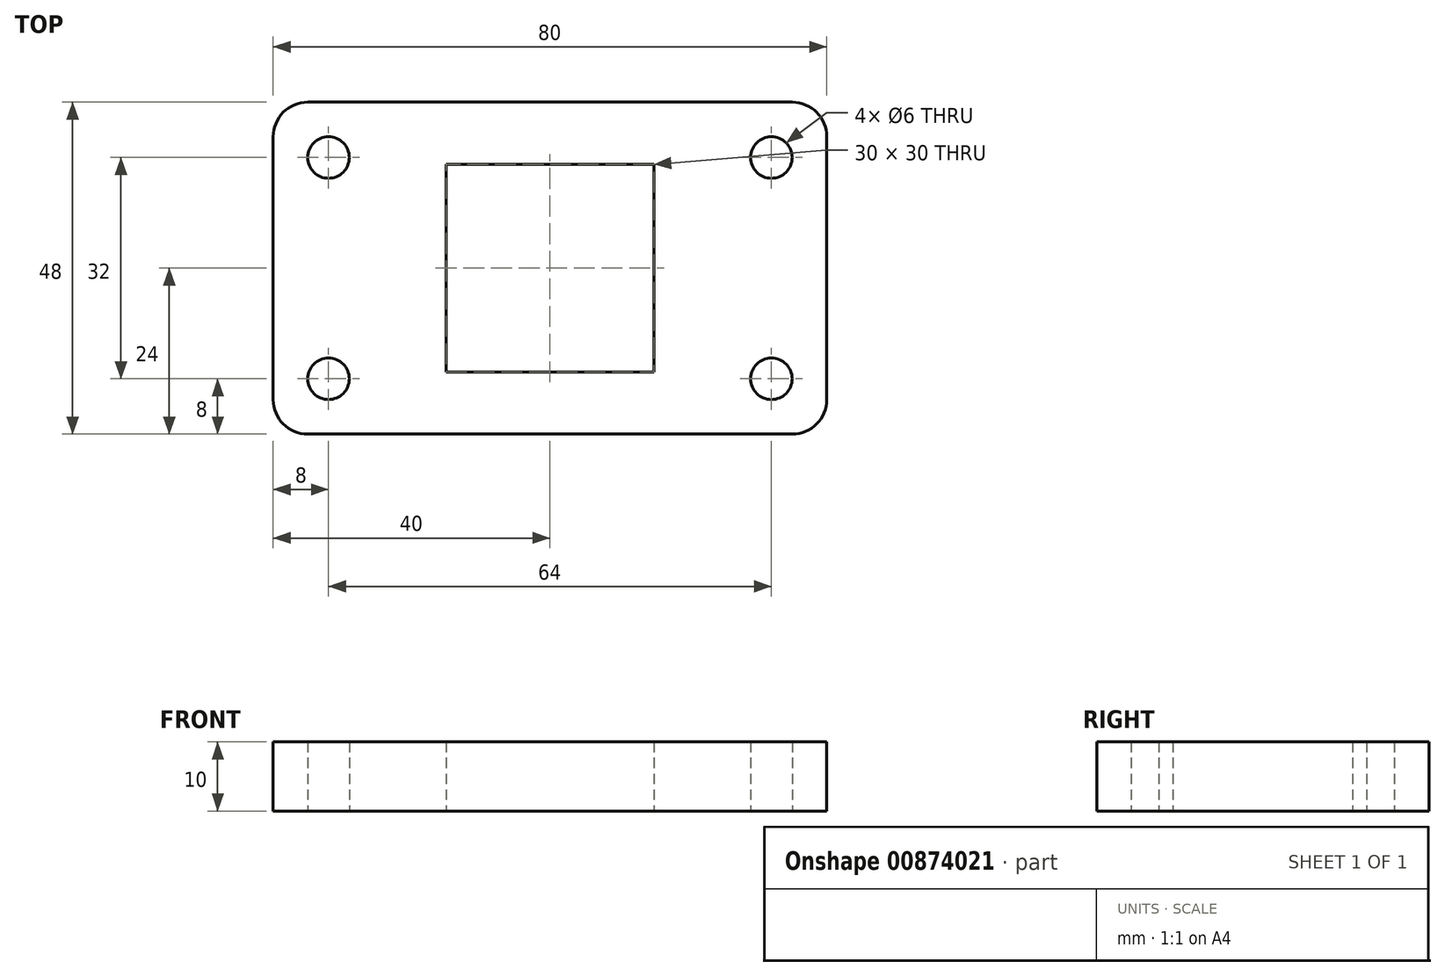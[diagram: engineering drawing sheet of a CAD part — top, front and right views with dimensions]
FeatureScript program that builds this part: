
annotation { "Feature Type Name" : "Feature", "Feature Type Description" : "" }
export const myFeature = defineFeature(function(context is Context, id is Id, definition is map)
    precondition{}
    {
        {
            var Q0;
            Q0=qCreatedBy(makeId("Top.planeOp"),FACE);
            var sketch = newSketch(context, id + "F0", { "sketchPlane" : qUnion([Q0])});
            skLineSegment(sketch, "E0.bottom", {"start": v(15, -15) * mm, "end": v(-15, -15) * mm});
            skLineSegment(sketch, "E0.top", {"start": v(15, 15) * mm, "end": v(-15, 15) * mm});
            skLineSegment(sketch, "E0.left", {"start": v(15, -15) * mm, "end": v(15, 15) * mm});
            skLineSegment(sketch, "E0.right", {"start": v(-15, -15) * mm, "end": v(-15, 15) * mm});
            skPoint(sketch, "E0.middle", {"position": v(0, 0) * mm});
            skLineSegment(sketch, "E1.bottom", {"start": v(3.97, -15) * mm, "end": v(-3.97, -15) * mm});
            skLineSegment(sketch, "E1.top", {"start": v(3.97, 15) * mm, "end": v(-3.97, 15) * mm});
            skLineSegment(sketch, "E1.left", {"start": v(3.97, -15) * mm, "end": v(3.97, 15) * mm});
            skLineSegment(sketch, "E1.right", {"start": v(-3.97, -15) * mm, "end": v(-3.97, 15) * mm});
            skLineSegment(sketch, "E2.bottom", {"start": v(40, -24) * mm, "end": v(-40, -24) * mm});
            skLineSegment(sketch, "E2.top", {"start": v(40, 24) * mm, "end": v(-40, 24) * mm});
            skLineSegment(sketch, "E2.left", {"start": v(40, -24) * mm, "end": v(40, 24) * mm});
            skLineSegment(sketch, "E2.right", {"start": v(-40, -24) * mm, "end": v(-40, 24) * mm});
            skPoint(sketch, "E3", {"position": v(32, 16) * mm});
            skCircle(sketch, "E4", {"center": v(32, 16) * mm, "radius": 3 * mm});
            skPoint(sketch, "E5", {"position": v(32, -16) * mm});
            skPoint(sketch, "E6", {"position": v(-32, -16) * mm});
            skPoint(sketch, "E7", {"position": v(-32, 16) * mm});
            skCircle(sketch, "E8", {"center": v(0, 0) * mm, "radius": 27 * mm});
            skLineSegment(sketch, "E9", {"start": v(0, 0) * mm, "end": v(27, 0) * mm});
            skPoint(sketch, "E9.endSnap0", {"position": v(15, 0) * mm});
            skPoint(sketch, "E10", {"position": v(32, 9) * mm});
            skLineSegment(sketch, "E11", {"start": v(0, 0) * mm, "end": v(32, 9) * mm});
            skPoint(sketch, "E12", {"position": v(0, -19.5) * mm});
            skSolve(sketch);
        }
        {
            var Q0;
            {var subQ0=sQuery(id+"F0.wireOp",EDGE,"E2.right");Q0=makeQuery(id+"F0.imprint","IMPRINT",FACE,{"disambiguationData":[TD([[makeQuery(id+"F0.imprint","IMPRINT",EDGE,{"derivedFrom":subQ0}),-1.0]])]});}
            var Q1;
            {var subQ7=sQuery(id+"F0.wireOp",EDGE,"E0.right");Q1=makeQuery(id+"F0.imprint","IMPRINT",FACE,{"disambiguationData":[TD([[makeQuery(id+"F0.imprint","IMPRINT",EDGE,{"derivedFrom":subQ7}),1.0]])]});}
            var Q2;
            {var subQ0=sQuery(id+"F0.wireOp",EDGE,"E9");var subQ1=sQuery(id+"F0.wireOp",EDGE,"E0.left");var subQ2=makeQuery(id+"F0.imprint","INTERSECT",VERTEX,{"derivedFrom":[subQ1,subQ0]});Q2=makeQuery(id+"F0.imprint","IMPRINT",FACE,{"disambiguationData":[TD([[makeQuery(id+"F0.imprint","IMPRINT",EDGE,{"disambiguationData":[TD([[subQ2,-1.0]])],"derivedFrom":subQ1}),-1.0]])]});}
            var Q3;
            {var subQ0=sQuery(id+"F0.wireOp",EDGE,"E2.left");Q3=makeQuery(id+"F0.imprint","IMPRINT",FACE,{"disambiguationData":[TD([[makeQuery(id+"F0.imprint","IMPRINT",EDGE,{"derivedFrom":subQ0}),1.0]])]});}
            var Q4;
            Q4=makeQuery(id+"F0.imprint","IMPRINT",FACE,{"disambiguationData":[TD([[makeQuery(id+"F0.imprint","IMPRINT",EDGE,{"derivedFrom":sQuery(id+"F0.wireOp",EDGE,"E4")}),1.0]])]});
            extrude(context, id + "F1", {"entities" : qUnion([Q0, Q1, Q2, Q3, Q4]), "depth" : 10 * mm, "offsetDistance" : 25 * mm});
        }
        {
            var Q0;
            Q0=makeQuery(id+"F1.opExtrude","SWEPT_EDGE",EDGE,{"disambiguationData":[OSD([sQuery(id+"F0.wireOp",EDGE,"E2.top"),sQuery(id+"F0.wireOp",EDGE,"E2.left")])]});
            var Q1;
            Q1=makeQuery(id+"F1.opExtrude","SWEPT_EDGE",EDGE,{"disambiguationData":[OSD([sQuery(id+"F0.wireOp",EDGE,"E2.bottom"),sQuery(id+"F0.wireOp",EDGE,"E2.left")])]});
            var Q2;
            Q2=makeQuery(id+"F1.opExtrude","SWEPT_EDGE",EDGE,{"disambiguationData":[OSD([sQuery(id+"F0.wireOp",EDGE,"E2.top"),sQuery(id+"F0.wireOp",EDGE,"E2.right")])]});
            var Q3;
            Q3=makeQuery(id+"F1.opExtrude","SWEPT_EDGE",EDGE,{"disambiguationData":[OSD([sQuery(id+"F0.wireOp",EDGE,"E2.bottom"),sQuery(id+"F0.wireOp",EDGE,"E2.right")])]});
            fillet(context, id + "F2", {"entities" : qUnion([Q0, Q1, Q2, Q3]), "radius" : 5 * mm, "tangentPropagation" : true, "allowEdgeOverflow" : false});
        }
        {
            var Q0;
            Q0=sQuery(id+"F0.wireOp",VERTEX,"E3");
            var Q1;
            Q1=sQuery(id+"F0.wireOp",VERTEX,"E5");
            var Q2;
            Q2=sQuery(id+"F0.wireOp",VERTEX,"E7");
            var Q3;
            Q3=sQuery(id+"F0.wireOp",VERTEX,"E6");
            var Q4;
            Q4=makeQuery(id+"F1.opExtrude","SWEPT_BODY",BODY,{"disambiguationData":[OSD([sQuery(id+"F0.wireOp",EDGE,"E0.bottom"),sQuery(id+"F0.wireOp",EDGE,"E0.top"),sQuery(id+"F0.wireOp",EDGE,"E0.left"),sQuery(id+"F0.wireOp",EDGE,"E0.right"),sQuery(id+"F0.wireOp",EDGE,"E1.bottom"),sQuery(id+"F0.wireOp",EDGE,"E1.top"),sQuery(id+"F0.wireOp",EDGE,"E2.bottom"),sQuery(id+"F0.wireOp",EDGE,"E2.top"),sQuery(id+"F0.wireOp",EDGE,"E2.left"),sQuery(id+"F0.wireOp",EDGE,"E2.right")])]});
            hole(context, id + "F3", {"style" : HoleStyle.SIMPLE, "endStyle" : HoleEndStyle.THROUGH, "oppositeDirection" : true, "standardTappedOrClearance" : lookupTablePath({ "standard" : "ISO", "size" : "6", "type" : "Drilled" }), "standardBlindInLast" : lookupTablePath({ "standard" : "ISO", "size" : "6", "type" : "Drilled" }), "holeDiameter" : 6 * mm, "majorDiameter" : 5 * mm, "isTappedThrough" : true, "tappedDepth" : 12 * mm, "tapClearance" : 3, "locations" : qUnion([Q0, Q1, Q2, Q3]), "scope" : qUnion([Q4])});
        }
    });
